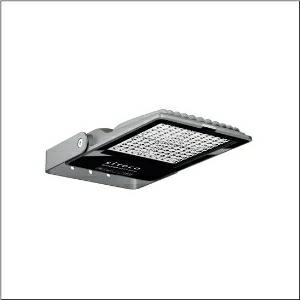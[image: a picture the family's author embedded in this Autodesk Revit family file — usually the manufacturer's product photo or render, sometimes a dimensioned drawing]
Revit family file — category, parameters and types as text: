
# Revit family: sicompact_r__31_mini___pl32_5xa7571b1k23_124a
name_source: partatom
category: Lighting Fixtures
units: mm (PartAtom-declared; Revit-internal decimal feet)

## family parameters
Cut with Voids When Loaded = No
Host = Face
Light Source = No
Part Type = Normal
Room Calculation Point = No
Round Connector Dimension = Use Diameter
Shared = No

## types (1)
- SiCompact® 31 mini  PL32 (1 x LED, 8000 lm, 48 W, 3000K)
    Apparent Load = 48 VA
    CIE Flux Codes = 32 69 98 100 100
    Color Rendering = 70
    Color Temperature = 3000K
    Default Elevation = 1800 mm
    Description = SiCompact® 31 mini, floodlight, primary light control with lens, of plastic, of toughened safety glass, transparent, light distribution: PL32, light emission: direct distribution, primary light characteristic: asymmetric, installation type: surface-mounted, LED, High Power LED, rated luminous flux: 8.000lm, luminous efficacy: 167lm/W, light colour: 730, colour temperature: 3000K, control gear: ECG, with cable, 3x 1.5mm², mains connection: 220..240V, AC, 50/60Hz, connection cable pre-assembled, cable length: 2m, rated input power: 48W, of diecast aluminium, specular, metallic grey (RAL 9006), length: 461mm, width: 261mm, height: 62mm, bracket, of sheet steel, coated, metallic grey (RAL 9006), ON/OFF, protection rating (complete): IP66, insulation class (complete): insulation class I (protective earthing), certification: CE, impact resistance: IK08, permissible operating ambient temperature: -40..+45°C, packaging unit: 1 piece

Light Distribution: PL32
    Height = 62 mm  [stored 0.203412 ft]
    Lamp = 1 x LED
    Lamp Light Flux = 8000 lm
    Lamp Power = 48 W
    Lamp count = 1
    Length = 460 mm
    Luminous efficacy = 167 lm/W
    Manufacturer = Siteco
    ModVariant = No
    Model = 5XA7571B1K23
    Number of Poles = 1
    OnlyDefault = Yes
    Power Factor = 1
    Product Name = SiCompact® 31 mini | PL32
    Product group = floodlight | pylon top
    ProductGroupID = 6101
    Protection Class = Protection class I
    Protection Degree = IP 66
    RLX_Detail_Level = 1
    RlxData = <blob elided: 126797 chars, md5=8a3c7a9b>
    Socket = socket
    Standby Power = 0 W
    System Light Flux = 8000 lm
    System Power = 48 W
    Type Comments = Product without accessories
    Type Image = l_1006951.jpg
    URL = http://relux.com
    VarID = ---
    Voltage = 0 V
    Weight = 0.00 kg
    Width = 260 mm

note: [stored X ft] marks values corroborated as IEEE doubles in the binary element streams (Revit-internal decimal feet)

## geometry (parser evidence)
native form markers: Blend x4, Sweep x15
no freeform markers — native parametric forms only
